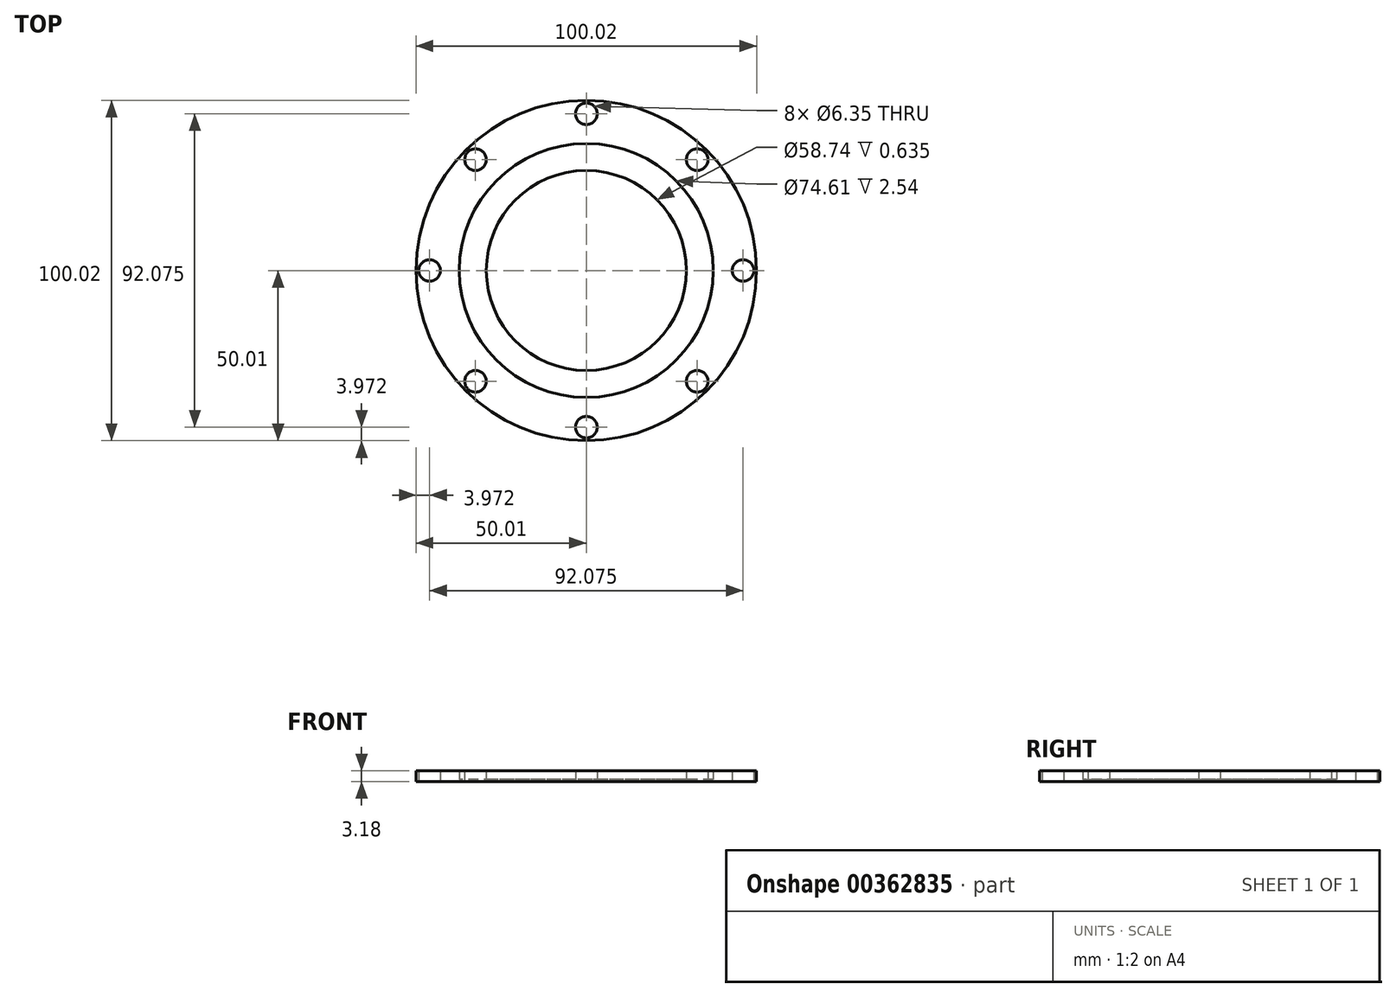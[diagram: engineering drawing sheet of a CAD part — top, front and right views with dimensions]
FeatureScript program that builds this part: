
annotation { "Feature Type Name" : "Feature", "Feature Type Description" : "" }
export const myFeature = defineFeature(function(context is Context, id is Id, definition is map)
    precondition{}
    {
        {
            var Q0;
            Q0=qCreatedBy(makeId("Top.planeOp"),FACE);
            var sketch = newSketch(context, id + "F0", { "sketchPlane" : qUnion([Q0])});
            skCircle(sketch, "E0", {"center": v(0, 0) * mm, "radius": 50 * mm});
            skCircle(sketch, "E1", {"center": v(0, 0) * mm, "radius": 37.3 * mm});
            skCircle(sketch, "E2", {"center": v(0, 0) * mm, "radius": 29.37 * mm});
            skCircle(sketch, "E3", {"center": v(0, 46.04) * mm, "radius": 3.18 * mm});
            skCircle(sketch, "E4", {"center": v(-32.55, 32.55) * mm, "radius": 3.18 * mm});
            skCircle(sketch, "E5", {"center": v(32.55, 32.55) * mm, "radius": 3.18 * mm});
            skCircle(sketch, "E6", {"center": v(46.04, 0) * mm, "radius": 3.18 * mm});
            skCircle(sketch, "E7", {"center": v(32.55, -32.55) * mm, "radius": 3.18 * mm});
            skCircle(sketch, "E8", {"center": v(0, -46.04) * mm, "radius": 3.18 * mm});
            skCircle(sketch, "E9", {"center": v(-32.55, -32.55) * mm, "radius": 3.18 * mm});
            skCircle(sketch, "E10", {"center": v(-46.04, 0) * mm, "radius": 3.18 * mm});
            skSolve(sketch);
        }
        {
            var Q0;
            Q0=makeQuery(id+"F0.imprint","IMPRINT",FACE,{"disambiguationData":[TD([[makeQuery(id+"F0.imprint","IMPRINT",EDGE,{"derivedFrom":sQuery(id+"F0.wireOp",EDGE,"E1")}),1.0]])]});
            extrude(context, id + "F1", {"entities" : qUnion([Q0]), "depth" : 0.64 * mm});
        }
        {
            var Q0;
            Q0 = qSketchRegion(id + "F0", true);
            extrude(context, id + "F2", {"entities" : qUnion([Q0]), "operationType" : NewBodyOperationType.ADD, "depth" : 3.17 * mm});
        }
    });
